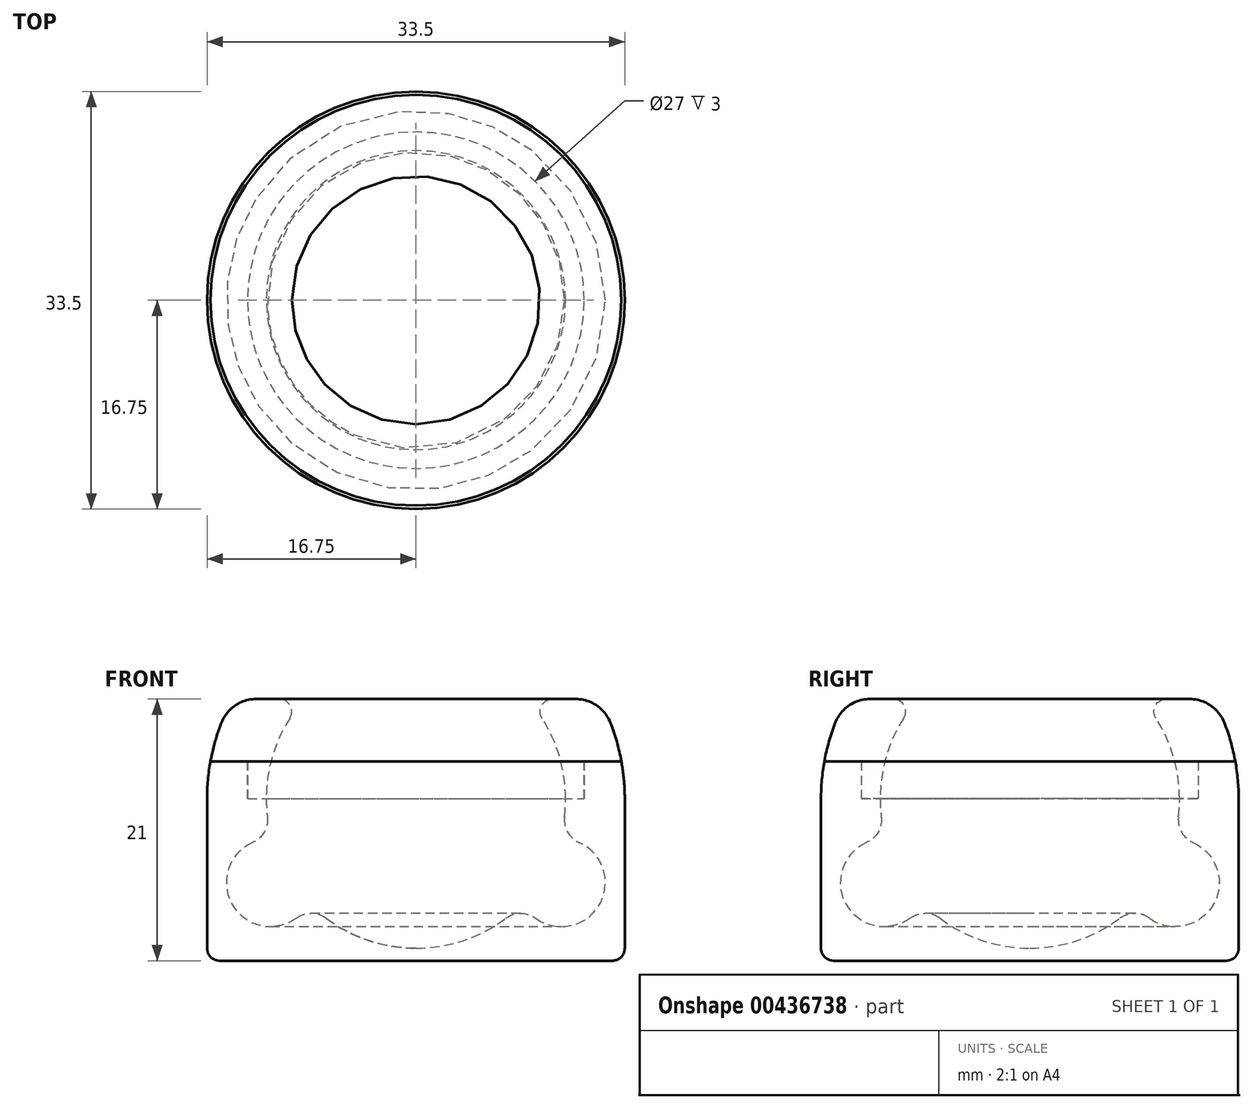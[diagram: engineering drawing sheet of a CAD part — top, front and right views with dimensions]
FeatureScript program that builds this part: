
annotation { "Feature Type Name" : "Feature", "Feature Type Description" : "" }
export const myFeature = defineFeature(function(context is Context, id is Id, definition is map)
    precondition{}
    {
        {
            var Q0;
            Q0=qCreatedBy(makeId("Front.planeOp"),FACE);
            var sketch = newSketch(context, id + "F0", { "sketchPlane" : qUnion([Q0])});
            skCircle(sketch, "E0", {"center": v(12.12, -7) * mm, "radius": 3 * mm, "construction": true});
            skCircle(sketch, "E1", {"center": v(0, 0) * mm, "radius": 11 * mm, "construction": true});
            skLineSegment(sketch, "E2", {"start": v(0, -15.87) * mm, "end": v(0, 12.8) * mm, "construction": true});
            skArc(sketch, "E3", {"start": v(8.56, -8.4) * mm, "mid": v(4.64, -11.07) * mm, "end": v(0, -12) * mm});
            skLineSegment(sketch, "E4", {"start": v(0, -12) * mm, "end": v(0, -13) * mm});
            skLineSegment(sketch, "E5", {"start": v(-0.91, 0.53) * mm, "end": v(15.94, -9.2) * mm, "construction": true});
            skLineSegment(sketch, "E6", {"start": v(0, -13) * mm, "end": v(16.75, -13) * mm});
            skLineSegment(sketch, "E7", {"start": v(16.75, -13) * mm, "end": v(16.75, 0) * mm});
            skLineSegment(sketch, "E8", {"start": v(12, 0) * mm, "end": v(13.5, 0) * mm});
            skLineSegment(sketch, "E9", {"start": v(13.5, 0) * mm, "end": v(13.5, 3) * mm});
            skArc(sketch, "E10", {"start": v(16.75, 0) * mm, "mid": v(16.68, 1.5) * mm, "end": v(16.48, 3) * mm});
            skLineSegment(sketch, "E11", {"start": v(13.5, 3) * mm, "end": v(16.48, 3) * mm});
            skArc(sketch, "E12", {"start": v(12, 0) * mm, "mid": v(11.9, -1.62) * mm, "end": v(11.56, -3.21) * mm});
            skArc(sketch, "E13", {"start": v(11.56, -3.21) * mm, "mid": v(14.72, -8.5) * mm, "end": v(8.56, -8.4) * mm});
            skLineSegment(sketch, "E14", {"start": v(6.88, -7.44) * mm, "end": v(13.45, -11.23) * mm, "construction": true});
            skLineSegment(sketch, "E15", {"start": v(9.22, -1.86) * mm, "end": v(16.04, -5.8) * mm, "construction": true});
            skSolve(sketch);
        }
        {
            var Q0;
            Q0 = qSketchRegion(id + "F0", true);
            var Q1;
            Q1=sQuery(id+"F0.wireOp",EDGE,"E2");
            revolve(context, id + "F1", {"entities" : qUnion([Q0]), "axis" : qUnion([Q1]), "revolveType" : RevolveType.FULL, "oppositeDirection" : true});
        }
        {
            var Q0;
            Q0=makeQuery(id+"F1.opRevolve","SWEPT_EDGE",EDGE,{"disambiguationData":[OSD([sQuery(id+"F0.wireOp",EDGE,"E3"),sQuery(id+"F0.wireOp",EDGE,"E13")])]});
            var Q1;
            Q1=makeQuery(id+"F1.opRevolve","SWEPT_EDGE",EDGE,{"disambiguationData":[OSD([sQuery(id+"F0.wireOp",EDGE,"E12"),sQuery(id+"F0.wireOp",EDGE,"E13")])]});
            fillet(context, id + "F2", {"entities" : qUnion([Q0, Q1]), "radius" : 2 * mm, "tangentPropagation" : true, "allowEdgeOverflow" : false});
        }
        {
            var Q0;
            Q0=qCreatedBy(makeId("Front.planeOp"),FACE);
            var sketch = newSketch(context, id + "F3", { "sketchPlane" : qUnion([Q0])});
            skArc(sketch, "E16", {"start": v(12, 0) * mm, "mid": v(11.21, 4.28) * mm, "end": v(8.94, 8) * mm});
            skLineSegment(sketch, "E17", {"start": v(8.94, 8) * mm, "end": v(8.94, 8) * mm});
            skLineSegment(sketch, "E18", {"start": v(8.94, 8) * mm, "end": v(14.71, 8) * mm});
            skLineSegment(sketch, "E19", {"start": v(13.5, 3) * mm, "end": v(16.48, 3) * mm});
            skLineSegment(sketch, "E20", {"start": v(13.5, 0) * mm, "end": v(13.5, 3) * mm});
            skLineSegment(sketch, "E21", {"start": v(12, 0) * mm, "end": v(13.5, 0) * mm});
            skArc(sketch, "E22", {"start": v(16.48, 3) * mm, "mid": v(15.8, 5.57) * mm, "end": v(14.71, 8) * mm});
            skSolve(sketch);
        }
        {
            var Q0;
            Q0 = qSketchRegion(id + "F3", true);
            var Q1;
            Q1=sQuery(id+"F0.wireOp",EDGE,"E2");
            revolve(context, id + "F4", {"entities" : qUnion([Q0]), "axis" : qUnion([Q1]), "revolveType" : RevolveType.FULL});
        }
        {
            var Q0;
            Q0=makeQuery(id+"F4.opRevolve","SWEPT_EDGE",EDGE,{"disambiguationData":[OSD([sQuery(id+"F3.wireOp",EDGE,"E16"),sQuery(id+"F3.wireOp",EDGE,"E18")])]});
            var Q1;
            Q1=makeQuery(id+"F1.opRevolve","SWEPT_EDGE",EDGE,{"disambiguationData":[OSD([sQuery(id+"F0.wireOp",EDGE,"E3"),sQuery(id+"F0.wireOp",EDGE,"NSIG349r-HCFJ-mytL-M4VM-UL1ARvsuJeLd")])]});
            var Q2;
            Q2=makeQuery(id+"F1.opRevolve","SWEPT_EDGE",EDGE,{"disambiguationData":[OSD([sQuery(id+"F0.wireOp",EDGE,"E6"),sQuery(id+"F0.wireOp",EDGE,"E7")])]});
            fillet(context, id + "F5", {"entities" : qUnion([Q0, Q1, Q2]), "radius" : 1 * mm, "tangentPropagation" : true, "allowEdgeOverflow" : false});
        }
        {
            var Q0;
            Q0=makeQuery(id+"F4.opRevolve","SWEPT_EDGE",EDGE,{"disambiguationData":[OSD([sQuery(id+"F3.wireOp",EDGE,"E18"),sQuery(id+"F3.wireOp",EDGE,"E22")])]});
            fillet(context, id + "F6", {"entities" : qUnion([Q0]), "radius" : 3 * mm, "tangentPropagation" : true, "allowEdgeOverflow" : false});
        }
    });
